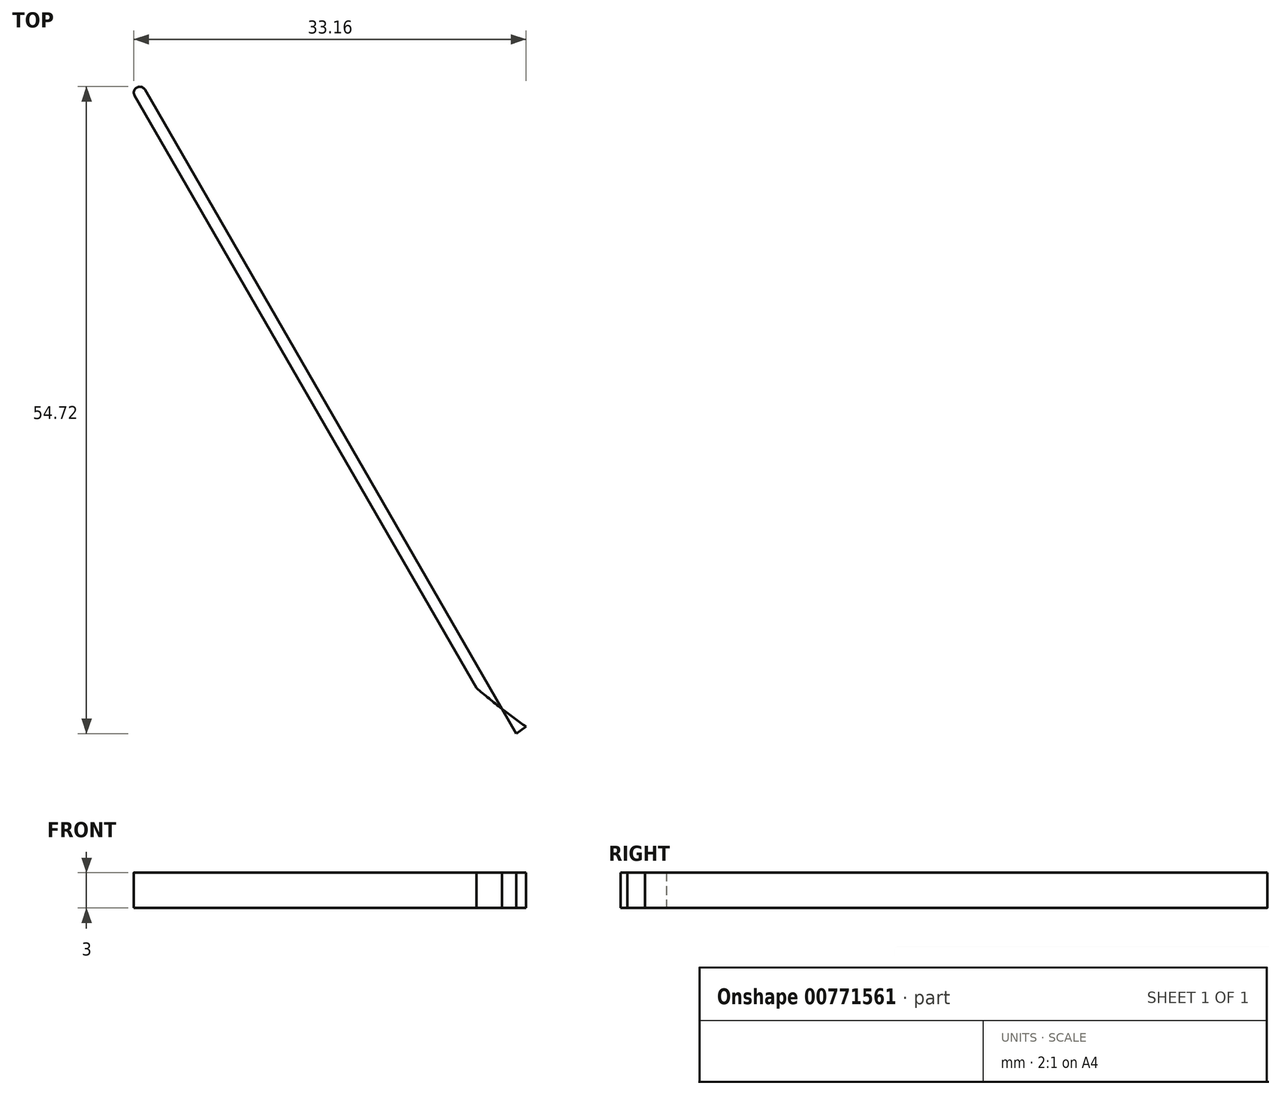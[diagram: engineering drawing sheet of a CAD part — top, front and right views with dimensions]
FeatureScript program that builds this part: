
annotation { "Feature Type Name" : "Feature", "Feature Type Description" : "" }
export const myFeature = defineFeature(function(context is Context, id is Id, definition is map)
    precondition{}
    {
        {
            var Q0;
            Q0=qCreatedBy(makeId("Top.planeOp"),FACE);
            var sketch = newSketch(context, id + "F0", { "sketchPlane" : qUnion([Q0])});
            skArc(sketch, "E0", {"start": v(-1.05, -2.9) * mm, "mid": v(3.06, -0.4) * mm, "end": v(-0.27, 3.07) * mm});
            skPoint(sketch, "E1", {"position": v(-24.96, 5.96) * mm});
            skLineSegment(sketch, "E2.0.startCap", {"start": v(-3.08, 2.46) * mm, "end": v(-3.08, 2.46) * mm});
            skFitSpline(sketch, "E2.0.right", {"points": [v(-2.67, 2.5) * mm, v(-5.5, 2.17) * mm, v(-11.3, 2.55) * mm, v(-18.7, 5.62) * mm, v(-24.55, 9.62) * mm, v(-28.86, 13.39) * mm, v(-33.04, 17.92) * mm, v(-38.47, 24.92) * mm, v(-45, 35.3) * mm, v(-52.5, 49.78) * mm, v(-59.8, 65.75) * mm, v(-64.62, 77.03) * mm, v(-67.04, 82.73) * mm]});
            skFitSpline(sketch, "E3", {"points": [v(-3.08, 2.46) * mm, v(-0.27, 3.07) * mm], "startDerivative": vector(4, 0.43) * mm, "endDerivative": vector(4.02, 0.35) * mm});
            skFitSpline(sketch, "E4", {"points": [v(-7.23, -0.55) * mm, v(-1.05, -2.9) * mm], "startDerivative": vector(9.7, -1.02) * mm, "endDerivative": vector(6.76, -2.44) * mm});
            skLineSegment(sketch, "E5", {"start": v(-24.63, 6.2) * mm, "end": v(-23.88, 6.73) * mm});
            skFitSpline(sketch, "E6.trimOffspring", {"points": [v(-2.2, -0.45) * mm, v(-5.41, -0.82) * mm, v(-11.94, -0.38) * mm, v(-20.02, 3) * mm, v(-26.29, 7.28) * mm, v(-30.85, 11.27) * mm, v(-35.23, 16.02) * mm, v(-40.85, 23.26) * mm, v(-47.5, 33.85) * mm, v(-55.1, 48.5) * mm, v(-62.45, 64.57) * mm, v(-67.28, 75.88) * mm, v(-69.7, 81.59) * mm]});
            skPoint(sketch, "E7.startDerivative.orphan", {"position": v(-12.14, 0) * mm});
            skArc(sketch, "E8.0.endCap", {"start": v(-55.35, 61.28) * mm, "mid": v(-55.16, 61.96) * mm, "end": v(-54.48, 61.77) * mm});
            skLineSegment(sketch, "E8.0.left", {"start": v(-23.88, 6.73) * mm, "end": v(-55.35, 61.28) * mm});
            skLineSegment(sketch, "E8.0.right", {"start": v(-23.06, 7.31) * mm, "end": v(-54.48, 61.77) * mm});
            skLineSegment(sketch, "E9.trimOffspring", {"start": v(-23.06, 7.31) * mm, "end": v(-22.12, 7.99) * mm});
            skSolve(sketch);
        }
        {
            var Q0;
            Q0 = qSketchRegion(id + "F0", true);
            extrude(context, id + "F1", {"entities" : qUnion([Q0]), "endBound" : BoundingType.SYMMETRIC, "depth" : 3 * mm, "offsetDistance" : 25 * mm});
        }
        {
            var Q0;
            Q0=makeQuery(id+"F1.opExtrude","CAP_FACE",FACE,{"disambiguationData":[OSD([sQuery(id+"F0.wireOp",EDGE,"E0"),sQuery(id+"F0.wireOp",EDGE,"E2.0.right"),sQuery(id+"F0.wireOp",EDGE,"E3"),sQuery(id+"F0.wireOp",EDGE,"E4"),sQuery(id+"F0.wireOp",EDGE,"E5"),sQuery(id+"F0.wireOp",EDGE,"E6.trimOffspring"),sQuery(id+"F0.wireOp",EDGE,"E8.0.endCap"),sQuery(id+"F0.wireOp",EDGE,"E8.0.left"),sQuery(id+"F0.wireOp",EDGE,"E8.0.right"),sQuery(id+"F0.wireOp",EDGE,"E9.trimOffspring")])],"isStart":true});
            var sketch = newSketch(context, id + "F2", { "sketchPlane" : qUnion([Q0])});
            skCircle(sketch, "E10", {"center": v(0, 0) * mm, "radius": 1.5 * mm});
            skSolve(sketch);
        }
        {
            var Q0;
            Q0 = qSketchRegion(id + "F2", true);
            extrude(context, id + "F3", {"entities" : qUnion([Q0]), "operationType" : NewBodyOperationType.REMOVE, "oppositeDirection" : true, "depth" : 25 * mm, "offsetDistance" : 25 * mm});
        }
    });
